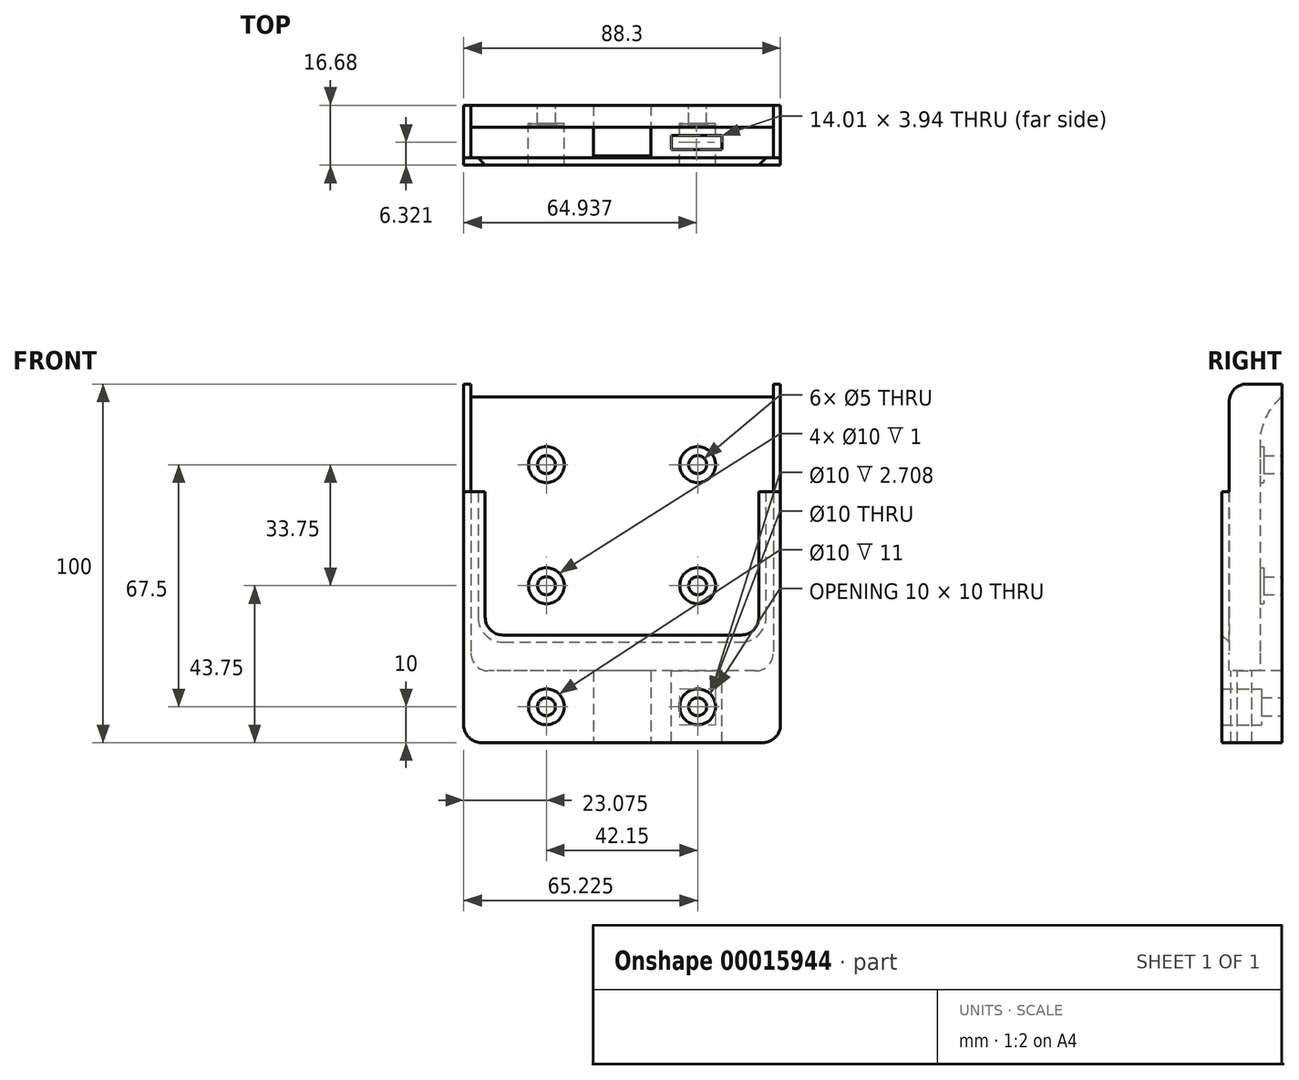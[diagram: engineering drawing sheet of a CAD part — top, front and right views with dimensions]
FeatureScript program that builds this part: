
annotation { "Feature Type Name" : "Feature", "Feature Type Description" : "" }
export const myFeature = defineFeature(function(context is Context, id is Id, definition is map)
    precondition{}
    {
        {
            var Q0;
            Q0=qCreatedBy(makeId("Right.planeOp"),FACE);
            var sketch = newSketch(context, id + "F0", { "sketchPlane" : qUnion([Q0])});
            skLineSegment(sketch, "E0", {"start": v(-10.6, -20) * mm, "end": v(6.08, -20) * mm});
            skLineSegment(sketch, "E1", {"start": v(6.08, -20) * mm, "end": v(6.08, 80) * mm});
            skLineSegment(sketch, "E2", {"start": v(6.08, 80) * mm, "end": v(-8.6, 80) * mm});
            skLineSegment(sketch, "E3", {"start": v(-10.6, 0) * mm, "end": v(-10.6, -20) * mm});
            skLineSegment(sketch, "E4", {"start": v(-10.6, 0) * mm, "end": v(-10.6, 50) * mm});
            skLineSegment(sketch, "E5", {"start": v(-10.6, 50) * mm, "end": v(-8.6, 50) * mm});
            skLineSegment(sketch, "E6", {"start": v(-8.6, 80) * mm, "end": v(-8.6, 50) * mm});
            skLineSegment(sketch, "E7", {"start": v(-10.6, 0) * mm, "end": v(0, 0) * mm, "construction": true});
            skLineSegment(sketch, "E8", {"start": v(4.08, 0) * mm, "end": v(6.08, 0) * mm, "construction": true});
            skLineSegment(sketch, "E9", {"start": v(0, 0) * mm, "end": v(0, 80) * mm, "construction": true});
            skSolve(sketch);
        }
        {
            var Q0;
            Q0=makeQuery(id+"F0.imprint","IMPRINT",FACE,{"disambiguationData":[TD([[makeQuery(id+"F0.imprint","IMPRINT",EDGE,{"derivedFrom":sQuery(id+"F0.wireOp",EDGE,"E0")}),1.0]])]});
            var Q1;
            {var subQ1=sQuery(id+"F0.wireOp",EDGE,"E4");Q1=makeQuery(id+"F0.imprint","IMPRINT",FACE,{"disambiguationData":[TD([[makeQuery(id+"F0.imprint","IMPRINT",EDGE,{"derivedFrom":subQ1}),-1.0]])]});}
            extrude(context, id + "F1", {"entities" : qUnion([Q0, Q1]), "depth" : 86.3 * mm, "hasSecondDirection" : true, "secondDirectionOppositeDirection" : true, "secondDirectionDepth" : 2 * mm});
        }
        {
            var Q0;
            Q0=qCreatedBy(makeId("Top.planeOp"),FACE);
            var sketch = newSketch(context, id + "F2", { "sketchPlane" : qUnion([Q0])});
            skLineSegment(sketch, "E10.rect.bottom", {"start": v(84.3, 0) * mm, "end": v(0, 0) * mm});
            skLineSegment(sketch, "E10.rect.top", {"start": v(84.3, -8.6) * mm, "end": v(0, -8.6) * mm});
            skLineSegment(sketch, "E10.rect.left", {"start": v(84.3, 0) * mm, "end": v(84.3, -8.6) * mm});
            skLineSegment(sketch, "E10.rect.right", {"start": v(0, 0) * mm, "end": v(0, -8.6) * mm});
            skPoint(sketch, "E10.rect.middle", {"position": v(0, 0) * mm});
            skSolve(sketch);
        }
        {
            var Q0;
            Q0=makeQuery(id+"F2.imprint","IMPRINT",FACE,{"disambiguationData":[TD([[makeQuery(id+"F2.imprint","IMPRINT",EDGE,{"derivedFrom":sQuery(id+"F2.wireOp",EDGE,"E10.rect.bottom")}),1.0]])]});
            extrude(context, id + "F3", {"entities" : qUnion([Q0]), "depth" : 156.2 * mm});
        }
        {
            var Q0;
            Q0=makeQuery(id+"F3.opExtrude","SWEPT_BODY",BODY,{"disambiguationData":[OSD([sQuery(id+"F2.wireOp",EDGE,"E10.rect.bottom"),sQuery(id+"F2.wireOp",EDGE,"E10.rect.top"),sQuery(id+"F2.wireOp",EDGE,"E10.rect.left"),sQuery(id+"F2.wireOp",EDGE,"E10.rect.right")])]});
            var Q1;
            Q1=makeQuery(id+"F1.opExtrude","SWEPT_BODY",BODY,{"disambiguationData":[OSD([sQuery(id+"F0.wireOp",EDGE,"E0"),sQuery(id+"F0.wireOp",EDGE,"E1"),sQuery(id+"F0.wireOp",EDGE,"E2"),sQuery(id+"F0.wireOp",EDGE,"E3"),sQuery(id+"F0.wireOp",EDGE,"E4"),sQuery(id+"F0.wireOp",EDGE,"E5"),sQuery(id+"F0.wireOp",EDGE,"E6")])]});
            booleanBodies(context, id + "F4", {"operationType" : BooleanOperationType.SUBTRACTION, "tools" : qUnion([Q0]), "targets" : qUnion([Q1])});
        }
        {
            var Q0;
            Q0=makeQuery(id+"F1.opExtrude","SWEPT_FACE",FACE,{"disambiguationData":[OSD([sQuery(id+"F0.wireOp",EDGE,"E3"),sQuery(id+"F0.wireOp",EDGE,"E4")])]});
            var sketch = newSketch(context, id + "F5", { "sketchPlane" : qUnion([Q0])});
            skPoint(sketch, "E11", {"position": v(0, 50) * mm});
            skPoint(sketch, "E12", {"position": v(84.3, 50) * mm});
            skLineSegment(sketch, "E13", {"start": v(0, 50) * mm, "end": v(4, 50) * mm, "construction": true});
            skLineSegment(sketch, "E14", {"start": v(84.3, 50) * mm, "end": v(80.3, 50) * mm, "construction": true});
            skPoint(sketch, "E15", {"position": v(4, -20) * mm});
            skLineSegment(sketch, "E16", {"start": v(4, -20) * mm, "end": v(4, 10) * mm, "construction": true});
            skPoint(sketch, "E17", {"position": v(80.3, -20) * mm});
            skLineSegment(sketch, "E18", {"start": v(80.3, -20) * mm, "end": v(80.3, 10) * mm, "construction": true});
            skLineSegment(sketch, "E19.bottom", {"start": v(4, 50) * mm, "end": v(80.3, 50) * mm});
            skLineSegment(sketch, "E19.top", {"start": v(4, 10) * mm, "end": v(80.3, 10) * mm});
            skLineSegment(sketch, "E19.left", {"start": v(4, 50) * mm, "end": v(4, 10) * mm});
            skLineSegment(sketch, "E19.right", {"start": v(80.3, 50) * mm, "end": v(80.3, 10) * mm});
            skSolve(sketch);
        }
        {
            var Q0;
            Q0 = qSketchRegion(id + "F5", true);
            extrude(context, id + "F6", {"entities" : qUnion([Q0]), "operationType" : NewBodyOperationType.REMOVE, "oppositeDirection" : true, "depth" : 8 * mm});
        }
        {
            var Q0;
            Q0=makeQuery(id+"F4.opBoolean","COPY",FACE,{"derivedFrom":makeQuery(id+"F3.opExtrude","CAP_FACE",FACE,{"disambiguationData":[OSD([sQuery(id+"F2.wireOp",EDGE,"E10.rect.bottom"),sQuery(id+"F2.wireOp",EDGE,"E10.rect.top"),sQuery(id+"F2.wireOp",EDGE,"E10.rect.left"),sQuery(id+"F2.wireOp",EDGE,"E10.rect.right")])],"isStart":true})});
            var sketch = newSketch(context, id + "F7", { "sketchPlane" : qUnion([Q0])});
            skPoint(sketch, "E20", {"position": v(42.15, 0) * mm});
            skPoint(sketch, "E21", {"position": v(0, -4.3) * mm});
            skPoint(sketch, "E22", {"position": v(42.15, -4.3) * mm});
            skLineSegment(sketch, "E23.rect.bottom", {"start": v(50.15, -0.55) * mm, "end": v(34.15, -0.55) * mm});
            skLineSegment(sketch, "E23.rect.top", {"start": v(50.15, -8.05) * mm, "end": v(34.15, -8.05) * mm});
            skLineSegment(sketch, "E23.rect.left", {"start": v(50.15, -0.55) * mm, "end": v(50.15, -8.05) * mm});
            skLineSegment(sketch, "E23.rect.right", {"start": v(34.15, -0.55) * mm, "end": v(34.15, -8.05) * mm});
            skLineSegment(sketch, "E24.bottom", {"start": v(34.15, -0.55) * mm, "end": v(50.15, -0.55) * mm});
            skLineSegment(sketch, "E24.top", {"start": v(34.15, 14.9) * mm, "end": v(50.15, 14.9) * mm});
            skLineSegment(sketch, "E24.left", {"start": v(34.15, -0.55) * mm, "end": v(34.15, 14.9) * mm});
            skLineSegment(sketch, "E24.right", {"start": v(50.15, -0.55) * mm, "end": v(50.15, 14.9) * mm});
            skSolve(sketch);
        }
        {
            var Q0;
            Q0 = qSketchRegion(id + "F7", true);
            extrude(context, id + "F8", {"entities" : qUnion([Q0]), "operationType" : NewBodyOperationType.REMOVE, "endBound" : BoundingType.THROUGH_ALL, "oppositeDirection" : true, "depth" : 25 * mm});
        }
        {
            var Q0;
            Q0=makeQuery(id+"F4.opBoolean","COPY",EDGE,{"derivedFrom":makeQuery(id+"F3.opExtrude","CAP_EDGE",EDGE,{"disambiguationData":[OSD([sQuery(id+"F2.wireOp",EDGE,"E10.rect.right")])],"isStart":true})});
            var Q1;
            Q1=makeQuery(id+"F4.opBoolean","COPY",EDGE,{"derivedFrom":makeQuery(id+"F3.opExtrude","CAP_EDGE",EDGE,{"disambiguationData":[OSD([sQuery(id+"F2.wireOp",EDGE,"E10.rect.left")])],"isStart":true})});
            var Q2;
            Q2=makeQuery(id+"F1.opExtrude","CAP_EDGE",EDGE,{"disambiguationData":[OSD([sQuery(id+"F0.wireOp",EDGE,"E0")])],"isStart":true});
            var Q3;
            Q3=makeQuery(id+"F1.opExtrude","CAP_EDGE",EDGE,{"disambiguationData":[OSD([sQuery(id+"F0.wireOp",EDGE,"E0")])],"isStart":false});
            var Q4;
            {var subQ0=sQuery(id+"F0.wireOp",EDGE,"E2");var subQ1=sQuery(id+"F0.wireOp",EDGE,"E6");Q4=makeQuery(id+"F4.opBoolean","SPLIT",EDGE,{"disambiguationData":[TD([makeQuery(id+"F3.opExtrude","SWEPT_FACE",FACE,{"disambiguationData":[OSD([sQuery(id+"F2.wireOp",EDGE,"E10.rect.right")])]})])],"derivedFrom":makeQuery(id+"F1.opExtrude","SWEPT_EDGE",EDGE,{"disambiguationData":[OSD([subQ0,subQ1])]})});}
            var Q5;
            {var subQ0=sQuery(id+"F0.wireOp",EDGE,"E2");var subQ1=sQuery(id+"F0.wireOp",EDGE,"E6");Q5=makeQuery(id+"F4.opBoolean","SPLIT",EDGE,{"disambiguationData":[TD([makeQuery(id+"F3.opExtrude","SWEPT_FACE",FACE,{"disambiguationData":[OSD([sQuery(id+"F2.wireOp",EDGE,"E10.rect.left")])]})])],"derivedFrom":makeQuery(id+"F1.opExtrude","SWEPT_EDGE",EDGE,{"disambiguationData":[OSD([subQ0,subQ1])]})});}
            var Q6;
            Q6=makeQuery(id+"F6.boolean.opBoolean","COPY",EDGE,{"derivedFrom":makeQuery(id+"F6.opExtrude","SWEPT_EDGE",EDGE,{"disambiguationData":[OSD([sQuery(id+"F0.wireOp",EDGE,"E4"),sQuery(id+"F0.wireOp",EDGE,"E5"),sQuery(id+"F5.wireOp",EDGE,"E19.bottom"),sQuery(id+"F5.wireOp",EDGE,"E19.left")])]})});
            var Q7;
            Q7=makeQuery(id+"F6.boolean.opBoolean","COPY",EDGE,{"derivedFrom":makeQuery(id+"F6.opExtrude","SWEPT_EDGE",EDGE,{"disambiguationData":[OSD([sQuery(id+"F0.wireOp",EDGE,"E4"),sQuery(id+"F0.wireOp",EDGE,"E5"),sQuery(id+"F5.wireOp",EDGE,"E19.bottom"),sQuery(id+"F5.wireOp",EDGE,"E19.right")])]})});
            var Q8;
            Q8=makeQuery(id+"F6.boolean.opBoolean","COPY",EDGE,{"derivedFrom":makeQuery(id+"F6.opExtrude","SWEPT_EDGE",EDGE,{"disambiguationData":[OSD([sQuery(id+"F5.wireOp",EDGE,"E19.top"),sQuery(id+"F5.wireOp",EDGE,"E19.left")])]})});
            var Q9;
            Q9=makeQuery(id+"F6.boolean.opBoolean","COPY",EDGE,{"derivedFrom":makeQuery(id+"F6.opExtrude","SWEPT_EDGE",EDGE,{"disambiguationData":[OSD([sQuery(id+"F5.wireOp",EDGE,"E19.top"),sQuery(id+"F5.wireOp",EDGE,"E19.right")])]})});
            fillet(context, id + "F9", {"entities" : qUnion([Q0, Q1, Q2, Q3, Q4, Q5, Q6, Q7, Q8, Q9]), "radius" : 5 * mm, "tangentPropagation" : true, "allowEdgeOverflow" : false});
        }
        {
            var Q0;
            Q0=makeQuery(id+"F6.boolean.opBoolean","INTERSECT",EDGE,{"derivedFrom":[makeQuery(id+"F4.opBoolean","COPY",FACE,{"derivedFrom":makeQuery(id+"F3.opExtrude","SWEPT_FACE",FACE,{"disambiguationData":[OSD([sQuery(id+"F2.wireOp",EDGE,"E10.rect.top")])]})}),makeQuery(id+"F6.opExtrude","SWEPT_FACE",FACE,{"disambiguationData":[OSD([sQuery(id+"F5.wireOp",EDGE,"E19.left")])]})]});
            var Q1;
            Q1=makeQuery(id+"F9.opFillet","BLEND_EDGE",EDGE,{"blendedFrom":[makeQuery(id+"F6.boolean.opBoolean","COPY",EDGE,{"derivedFrom":makeQuery(id+"F6.opExtrude","SWEPT_EDGE",EDGE,{"disambiguationData":[OSD([sQuery(id+"F5.wireOp",EDGE,"E19.top"),sQuery(id+"F5.wireOp",EDGE,"E19.left")])]})}),makeQuery(id+"F4.opBoolean","COPY",FACE,{"derivedFrom":makeQuery(id+"F3.opExtrude","SWEPT_FACE",FACE,{"disambiguationData":[OSD([sQuery(id+"F2.wireOp",EDGE,"E10.rect.top")])]})})],"blendedInto":[makeQuery(id+"F4.opBoolean","COPY",FACE,{"derivedFrom":makeQuery(id+"F3.opExtrude","SWEPT_FACE",FACE,{"disambiguationData":[OSD([sQuery(id+"F2.wireOp",EDGE,"E10.rect.top")])]})})]});
            var Q2;
            Q2=makeQuery(id+"F6.boolean.opBoolean","INTERSECT",EDGE,{"derivedFrom":[makeQuery(id+"F4.opBoolean","COPY",FACE,{"derivedFrom":makeQuery(id+"F3.opExtrude","SWEPT_FACE",FACE,{"disambiguationData":[OSD([sQuery(id+"F2.wireOp",EDGE,"E10.rect.top")])]})}),makeQuery(id+"F6.opExtrude","SWEPT_FACE",FACE,{"disambiguationData":[OSD([sQuery(id+"F5.wireOp",EDGE,"E19.top")])]})]});
            var Q3;
            Q3=makeQuery(id+"F9.opFillet","BLEND_EDGE",EDGE,{"blendedFrom":[makeQuery(id+"F6.boolean.opBoolean","COPY",EDGE,{"derivedFrom":makeQuery(id+"F6.opExtrude","SWEPT_EDGE",EDGE,{"disambiguationData":[OSD([sQuery(id+"F5.wireOp",EDGE,"E19.top"),sQuery(id+"F5.wireOp",EDGE,"E19.right")])]})}),makeQuery(id+"F4.opBoolean","COPY",FACE,{"derivedFrom":makeQuery(id+"F3.opExtrude","SWEPT_FACE",FACE,{"disambiguationData":[OSD([sQuery(id+"F2.wireOp",EDGE,"E10.rect.top")])]})})],"blendedInto":[makeQuery(id+"F4.opBoolean","COPY",FACE,{"derivedFrom":makeQuery(id+"F3.opExtrude","SWEPT_FACE",FACE,{"disambiguationData":[OSD([sQuery(id+"F2.wireOp",EDGE,"E10.rect.top")])]})})]});
            var Q4;
            Q4=makeQuery(id+"F6.boolean.opBoolean","INTERSECT",EDGE,{"derivedFrom":[makeQuery(id+"F4.opBoolean","COPY",FACE,{"derivedFrom":makeQuery(id+"F3.opExtrude","SWEPT_FACE",FACE,{"disambiguationData":[OSD([sQuery(id+"F2.wireOp",EDGE,"E10.rect.top")])]})}),makeQuery(id+"F6.opExtrude","SWEPT_FACE",FACE,{"disambiguationData":[OSD([sQuery(id+"F5.wireOp",EDGE,"E19.right")])]})]});
            var Q5;
            Q5=makeQuery(id+"F9.opFillet","BLEND_EDGE",EDGE,{"blendedFrom":[makeQuery(id+"F6.boolean.opBoolean","COPY",EDGE,{"derivedFrom":makeQuery(id+"F6.opExtrude","SWEPT_EDGE",EDGE,{"disambiguationData":[OSD([sQuery(id+"F0.wireOp",EDGE,"E4"),sQuery(id+"F0.wireOp",EDGE,"E5"),sQuery(id+"F5.wireOp",EDGE,"E19.bottom"),sQuery(id+"F5.wireOp",EDGE,"E19.right")])]})}),makeQuery(id+"F4.opBoolean","COPY",FACE,{"derivedFrom":makeQuery(id+"F3.opExtrude","SWEPT_FACE",FACE,{"disambiguationData":[OSD([sQuery(id+"F2.wireOp",EDGE,"E10.rect.top")])]})})],"blendedInto":[makeQuery(id+"F4.opBoolean","COPY",FACE,{"derivedFrom":makeQuery(id+"F3.opExtrude","SWEPT_FACE",FACE,{"disambiguationData":[OSD([sQuery(id+"F2.wireOp",EDGE,"E10.rect.top")])]})})]});
            var Q6;
            Q6=makeQuery(id+"F9.opFillet","BLEND_EDGE",EDGE,{"blendedFrom":[makeQuery(id+"F6.boolean.opBoolean","COPY",EDGE,{"derivedFrom":makeQuery(id+"F6.opExtrude","SWEPT_EDGE",EDGE,{"disambiguationData":[OSD([sQuery(id+"F0.wireOp",EDGE,"E4"),sQuery(id+"F0.wireOp",EDGE,"E5"),sQuery(id+"F5.wireOp",EDGE,"E19.bottom"),sQuery(id+"F5.wireOp",EDGE,"E19.left")])]})}),makeQuery(id+"F4.opBoolean","COPY",FACE,{"derivedFrom":makeQuery(id+"F3.opExtrude","SWEPT_FACE",FACE,{"disambiguationData":[OSD([sQuery(id+"F2.wireOp",EDGE,"E10.rect.top")])]})})],"blendedInto":[makeQuery(id+"F4.opBoolean","COPY",FACE,{"derivedFrom":makeQuery(id+"F3.opExtrude","SWEPT_FACE",FACE,{"disambiguationData":[OSD([sQuery(id+"F2.wireOp",EDGE,"E10.rect.top")])]})})]});
            chamfer(context, id + "F10", {"entities" : qUnion([Q0, Q1, Q2, Q3, Q4, Q5, Q6]), "width" : 2 * mm, "tangentPropagation" : true});
        }
        {
            var Q0;
            Q0=makeQuery(id+"F4.opBoolean","COPY",FACE,{"derivedFrom":makeQuery(id+"F3.opExtrude","SWEPT_FACE",FACE,{"disambiguationData":[OSD([sQuery(id+"F2.wireOp",EDGE,"E10.rect.bottom")])]})});
            var sketch = newSketch(context, id + "F11", { "sketchPlane" : qUnion([Q0])});
            skPoint(sketch, "E25", {"position": v(42.15, 72.5) * mm});
            skPoint(sketch, "E26", {"position": v(0, 42.5) * mm});
            skPoint(sketch, "E27", {"position": v(84.3, 42.5) * mm});
            skLineSegment(sketch, "E28", {"start": v(0, 42.5) * mm, "end": v(42.15, 42.5) * mm, "construction": true});
            skLineSegment(sketch, "E29", {"start": v(42.15, 42.5) * mm, "end": v(42.15, 72.5) * mm, "construction": true});
            skLineSegment(sketch, "E30", {"start": v(84.3, 42.5) * mm, "end": v(42.15, 42.5) * mm, "construction": true});
            skPoint(sketch, "E31", {"position": v(21.07, 42.5) * mm});
            skPoint(sketch, "E32", {"position": v(63.23, 42.5) * mm});
            skPoint(sketch, "E33", {"position": v(42.15, 57.5) * mm});
            skPoint(sketch, "E34", {"position": v(21.07, 57.5) * mm});
            skPoint(sketch, "E35", {"position": v(63.23, 57.5) * mm});
            skLineSegment(sketch, "E36", {"start": v(42.15, 42.5) * mm, "end": v(42.15, 5) * mm, "construction": true});
            skLineSegment(sketch, "E37", {"start": v(42.15, 5) * mm, "end": v(0, 5) * mm, "construction": true});
            skLineSegment(sketch, "E38", {"start": v(42.15, 5) * mm, "end": v(84.3, 5) * mm, "construction": true});
            skPoint(sketch, "E39", {"position": v(42.15, 23.75) * mm});
            skPoint(sketch, "E40", {"position": v(21.07, 23.75) * mm});
            skPoint(sketch, "E41", {"position": v(63.23, 23.75) * mm});
            skLineSegment(sketch, "E42", {"start": v(21.07, 57.5) * mm, "end": v(21.08, 23.75) * mm, "construction": true});
            skLineSegment(sketch, "E43", {"start": v(21.07, 23.75) * mm, "end": v(21.07, -10) * mm, "construction": true});
            skPoint(sketch, "E44", {"position": v(21.07, -10) * mm});
            skPoint(sketch, "E45", {"position": v(63.23, -10) * mm});
            skSolve(sketch);
        }
        {
            var Q0;
            Q0=sQuery(id+"F11.wireOp",VERTEX,"E34");
            var Q1;
            Q1=sQuery(id+"F11.wireOp",VERTEX,"E35");
            var Q2;
            Q2=sQuery(id+"F11.wireOp",VERTEX,"E41");
            var Q3;
            Q3=sQuery(id+"F11.wireOp",VERTEX,"E40");
            var Q4;
            Q4=makeQuery(id+"F1.opExtrude","SWEPT_BODY",BODY,{"disambiguationData":[OSD([sQuery(id+"F0.wireOp",EDGE,"E0"),sQuery(id+"F0.wireOp",EDGE,"E1"),sQuery(id+"F0.wireOp",EDGE,"E2"),sQuery(id+"F0.wireOp",EDGE,"E3"),sQuery(id+"F0.wireOp",EDGE,"E4"),sQuery(id+"F0.wireOp",EDGE,"E5"),sQuery(id+"F0.wireOp",EDGE,"E6")])]});
            hole(context, id + "F12", {"style" : HoleStyle.C_BORE, "holeDiameter" : 5 * mm, "cBoreDiameter" : 10 * mm, "cBoreDepth" : 1 * mm, "endStyle" : HoleEndStyle.THROUGH, "locations" : qUnion([Q0, Q1, Q2, Q3]), "scope" : qUnion([Q4])});
        }
        {
            var Q0;
            Q0=makeQuery(id+"F1.opExtrude","SWEPT_FACE",FACE,{"disambiguationData":[OSD([sQuery(id+"F0.wireOp",EDGE,"E3"),sQuery(id+"F0.wireOp",EDGE,"E4")])]});
            var sketch = newSketch(context, id + "F13", { "sketchPlane" : qUnion([Q0])});
            skPoint(sketch, "E46", {"position": v(63.23, -10) * mm});
            skPoint(sketch, "E47", {"position": v(21.07, -10) * mm});
            skSolve(sketch);
        }
        {
            var Q0;
            Q0=sQuery(id+"F13.wireOp",VERTEX,"E47");
            var Q1;
            Q1=sQuery(id+"F13.wireOp",VERTEX,"E46");
            var Q2;
            Q2=makeQuery(id+"F1.opExtrude","SWEPT_BODY",BODY,{"disambiguationData":[OSD([sQuery(id+"F0.wireOp",EDGE,"E0"),sQuery(id+"F0.wireOp",EDGE,"E1"),sQuery(id+"F0.wireOp",EDGE,"E2"),sQuery(id+"F0.wireOp",EDGE,"E3"),sQuery(id+"F0.wireOp",EDGE,"E4"),sQuery(id+"F0.wireOp",EDGE,"E5"),sQuery(id+"F0.wireOp",EDGE,"E6")])]});
            hole(context, id + "F14", {"style" : HoleStyle.C_BORE, "holeDiameter" : 5 * mm, "cBoreDiameter" : 10 * mm, "cBoreDepth" : 11 * mm, "endStyle" : HoleEndStyle.THROUGH, "locations" : qUnion([Q0, Q1]), "scope" : qUnion([Q2])});
        }
        {
            var Q0;
            Q0=makeQuery(id+"F4.opBoolean","INTERSECT",EDGE,{"derivedFrom":[makeQuery(id+"F1.opExtrude","SWEPT_FACE",FACE,{"disambiguationData":[OSD([sQuery(id+"F0.wireOp",EDGE,"E2")])]}),makeQuery(id+"F3.opExtrude","SWEPT_FACE",FACE,{"disambiguationData":[OSD([sQuery(id+"F2.wireOp",EDGE,"E10.rect.bottom")])]})]});
            fillet(context, id + "F15", {"entities" : qUnion([Q0]), "radius" : 16.4 * mm, "tangentPropagation" : true, "allowEdgeOverflow" : false});
        }
        {
            var Q0;
            Q0=makeQuery(id+"F4.opBoolean","COPY",FACE,{"derivedFrom":makeQuery(id+"F3.opExtrude","CAP_FACE",FACE,{"disambiguationData":[OSD([sQuery(id+"F2.wireOp",EDGE,"E10.rect.bottom"),sQuery(id+"F2.wireOp",EDGE,"E10.rect.top"),sQuery(id+"F2.wireOp",EDGE,"E10.rect.left"),sQuery(id+"F2.wireOp",EDGE,"E10.rect.right")])],"isStart":true})});
            var sketch = newSketch(context, id + "F16", { "sketchPlane" : qUnion([Q0])});
            skLineSegment(sketch, "E48.bottom", {"start": v(55.93, -6.25) * mm, "end": v(69.94, -6.25) * mm});
            skLineSegment(sketch, "E48.top", {"start": v(55.93, -2.3) * mm, "end": v(69.94, -2.3) * mm});
            skLineSegment(sketch, "E48.left", {"start": v(55.93, -6.25) * mm, "end": v(55.93, -2.3) * mm});
            skLineSegment(sketch, "E48.right", {"start": v(69.94, -6.25) * mm, "end": v(69.94, -2.3) * mm});
            skSolve(sketch);
        }
        {
            var Q0;
            Q0 = qSketchRegion(id + "F16", true);
            extrude(context, id + "F17", {"entities" : qUnion([Q0]), "operationType" : NewBodyOperationType.REMOVE, "endBound" : BoundingType.THROUGH_ALL, "oppositeDirection" : true, "depth" : 25 * mm});
        }
    });
